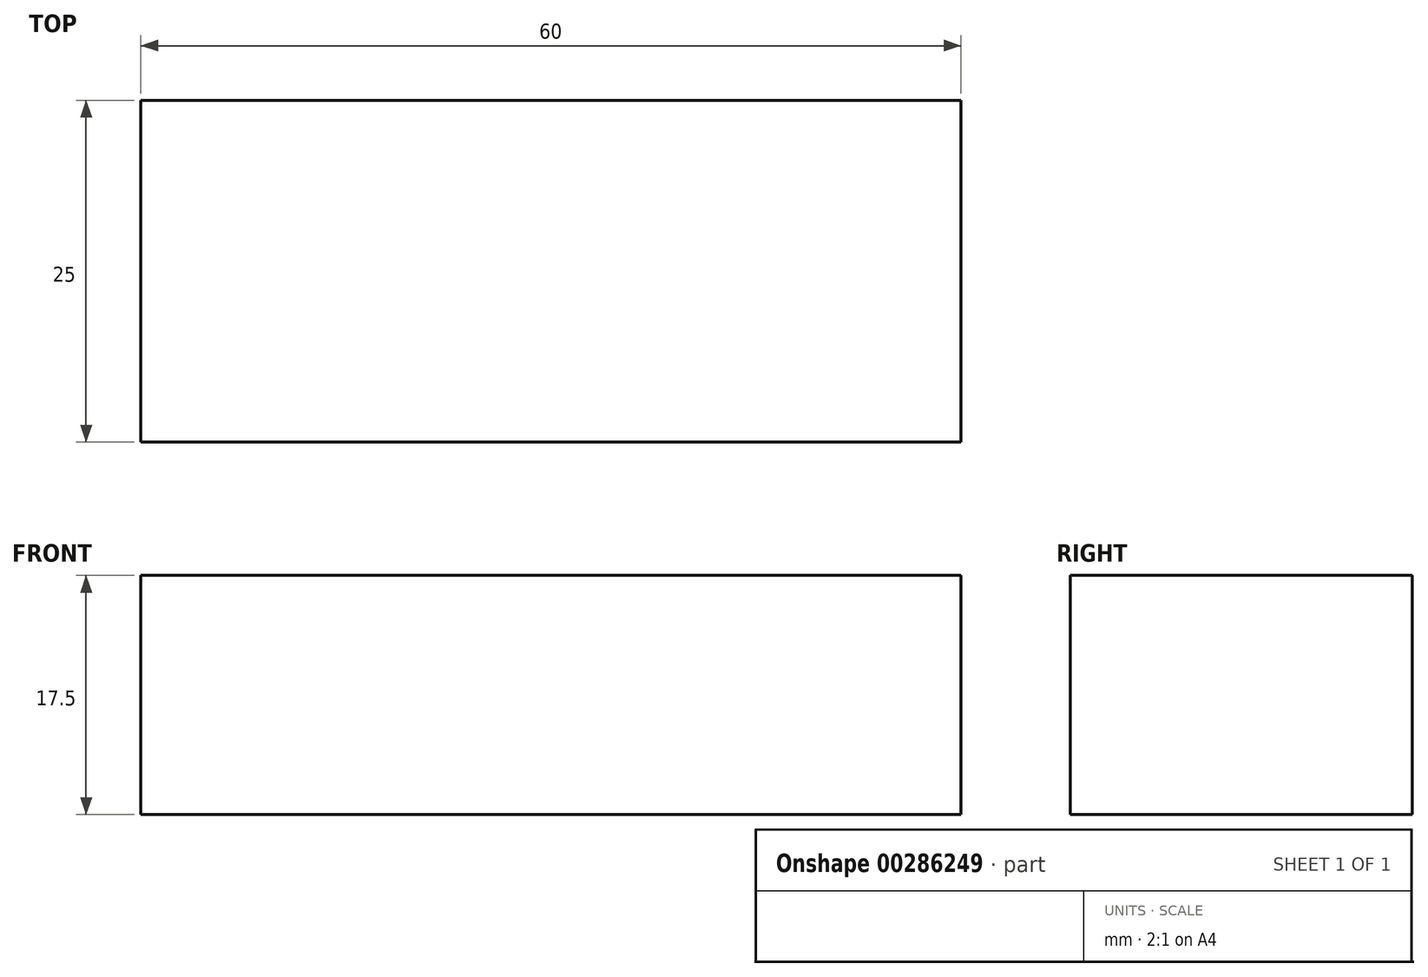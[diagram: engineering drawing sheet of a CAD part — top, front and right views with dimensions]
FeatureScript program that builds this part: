
annotation { "Feature Type Name" : "Feature", "Feature Type Description" : "" }
export const myFeature = defineFeature(function(context is Context, id is Id, definition is map)
    precondition{}
    {
        {
            var Q0;
            Q0=qCreatedBy(makeId("Front.planeOp"),FACE);
            var sketch = newSketch(context, id + "F0", { "sketchPlane" : qUnion([Q0])});
            skLineSegment(sketch, "E0.bottom", {"start": v(0, 0) * mm, "end": v(60, 0) * mm});
            skLineSegment(sketch, "E0.top", {"start": v(0, 17.5) * mm, "end": v(60, 17.5) * mm});
            skLineSegment(sketch, "E0.left", {"start": v(0, 0) * mm, "end": v(0, 17.5) * mm});
            skLineSegment(sketch, "E0.right", {"start": v(60, 0) * mm, "end": v(60, 17.5) * mm});
            skSolve(sketch);
        }
        {
            var Q0;
            Q0=qSketchRegion(id+"F0",true);
            extrude(context, id + "F1", {"entities" : qUnion([Q0]), "depth" : 25 * mm});
        }
    });
